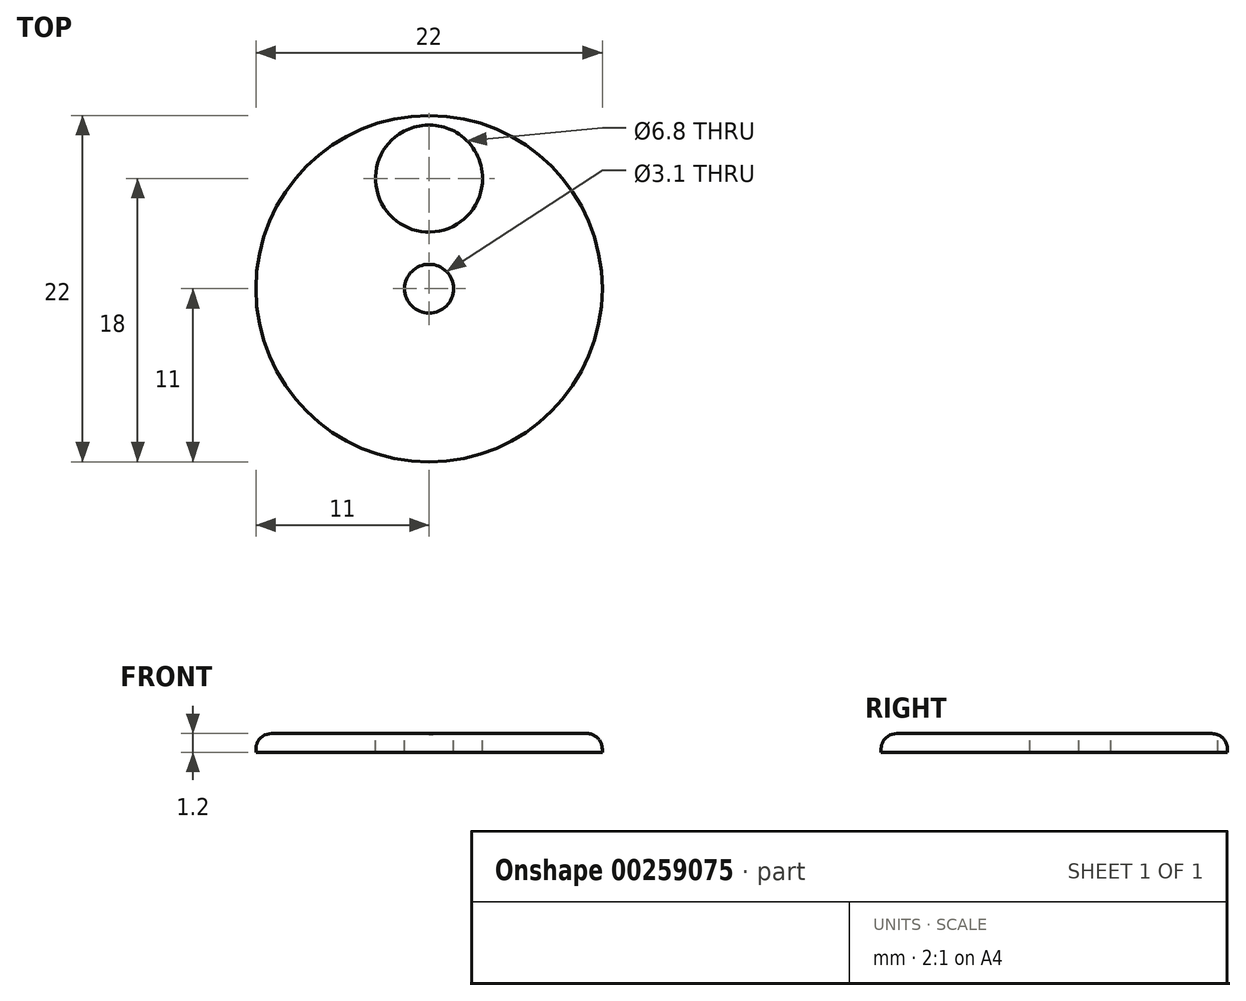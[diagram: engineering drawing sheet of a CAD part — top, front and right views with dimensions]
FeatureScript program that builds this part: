
annotation { "Feature Type Name" : "Feature", "Feature Type Description" : "" }
export const myFeature = defineFeature(function(context is Context, id is Id, definition is map)
    precondition{}
    {
        {
            var Q0;
            Q0=qCreatedBy(makeId("Top.planeOp"),FACE);
            var sketch = newSketch(context, id + "F0", { "sketchPlane" : qUnion([Q0])});
            skCircle(sketch, "E0", {"center": v(0, 0) * mm, "radius": 11 * mm});
            skSolve(sketch);
        }
        {
            var Q0;
            Q0 = qSketchRegion(id + "F0", true);
            extrude(context, id + "F1", {"entities" : qUnion([Q0]), "depth" : 1.2 * mm});
        }
        {
            var Q0;
            Q0=makeQuery(id+"F1.opExtrude","CAP_EDGE",EDGE,{"disambiguationData":[OSD([sQuery(id+"F0.wireOp",EDGE,"E0")])],"isStart":false});
            fillet(context, id + "F2", {"entities" : qUnion([Q0]), "radius" : 1 * mm, "tangentPropagation" : true, "allowEdgeOverflow" : false});
        }
        {
            var Q0;
            Q0=makeQuery(id+"F1.opExtrude","CAP_FACE",FACE,{"disambiguationData":[OSD([sQuery(id+"F0.wireOp",EDGE,"E0")])],"isStart":false});
            var sketch = newSketch(context, id + "F3", { "sketchPlane" : qUnion([Q0])});
            skCircle(sketch, "E1", {"center": v(0, 0) * mm, "radius": 1.55 * mm});
            skCircle(sketch, "E2", {"center": v(0, 7) * mm, "radius": 3.4 * mm});
            skSolve(sketch);
        }
        {
            var Q0;
            Q0 = qSketchRegion(id + "F3", true);
            extrude(context, id + "F4", {"entities" : qUnion([Q0]), "operationType" : NewBodyOperationType.REMOVE, "oppositeDirection" : true, "depth" : 25 * mm});
        }
    });
